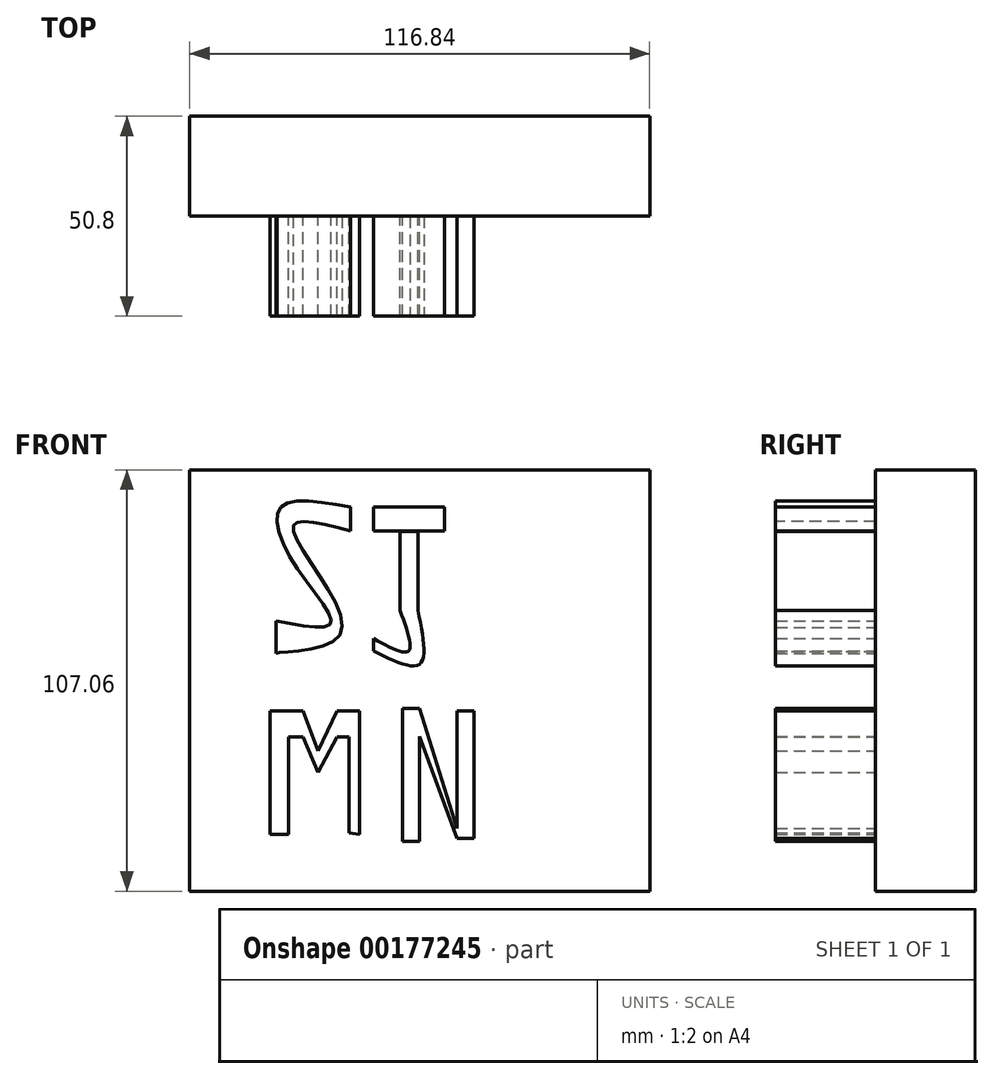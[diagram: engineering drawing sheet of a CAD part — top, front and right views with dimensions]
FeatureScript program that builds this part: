
annotation { "Feature Type Name" : "Feature", "Feature Type Description" : "" }
export const myFeature = defineFeature(function(context is Context, id is Id, definition is map)
    precondition{}
    {
        {
            var Q0;
            Q0=qCreatedBy(makeId("Front.planeOp"),FACE);
            var sketch = newSketch(context, id + "F0", { "sketchPlane" : qUnion([Q0])});
            skLineSegment(sketch, "E0.bottom", {"start": v(-58.42, -53.53) * mm, "end": v(58.42, -53.53) * mm});
            skLineSegment(sketch, "E0.top", {"start": v(-58.42, 53.53) * mm, "end": v(58.42, 53.53) * mm});
            skLineSegment(sketch, "E0.left", {"start": v(-58.42, -53.53) * mm, "end": v(-58.42, 53.53) * mm});
            skLineSegment(sketch, "E0.right", {"start": v(58.42, -53.53) * mm, "end": v(58.42, 53.53) * mm});
            skPoint(sketch, "E0.middle", {"position": v(0, 0) * mm});
            skSolve(sketch);
        }
        {
            var Q0;
            Q0 = qSketchRegion(id + "F0", true);
            extrude(context, id + "F1", {"entities" : qUnion([Q0]), "depth" : 25.4 * mm});
        }
        {
            var Q0;
            Q0=makeQuery(id+"F1.opExtrude","CAP_FACE",FACE,{"disambiguationData":[OSD([sQuery(id+"F0.wireOp",EDGE,"E0.bottom"),sQuery(id+"F0.wireOp",EDGE,"E0.top"),sQuery(id+"F0.wireOp",EDGE,"E0.left"),sQuery(id+"F0.wireOp",EDGE,"E0.right")])],"isStart":false});
            var sketch = newSketch(context, id + "F2", { "sketchPlane" : qUnion([Q0])});
            skFitSpline(sketch, "E1", {"points": [v(-17.56, 38) * mm, v(-32.23, 38.57) * mm, v(-20.15, 11.8) * mm, v(-36.55, 6.9) * mm, v(-36.26, 6.62) * mm], "startDerivative": vector(-81.22, 21.83) * mm, "endDerivative": vector(12.9, -6.86) * mm});
            skLineSegment(sketch, "E2", {"start": v(-17.56, 38) * mm, "end": v(-17.56, 44.03) * mm});
            skLineSegment(sketch, "E3", {"start": v(-36.55, 6.9) * mm, "end": v(-36.55, 15.16) * mm});
            skPoint(sketch, "E4.1.internal.orphan", {"position": v(-35.28, 44.03) * mm});
            skFitSpline(sketch, "E5", {"points": [v(-17.56, 44.03) * mm, v(-35.28, 44.03) * mm, v(-31.96, 29.73) * mm, v(-22.6, 14.54) * mm, v(-36.55, 15.16) * mm], "startDerivative": vector(-86.65, 15.67) * mm, "endDerivative": vector(-84.04, 16.75) * mm});
            skSolve(sketch);
        }
        {
            var Q0;
            {var subQ0=sQuery(id+"F2.wireOp",EDGE,"E2");Q0=makeQuery(id+"F2.imprint","IMPRINT",FACE,{"disambiguationData":[TD([[makeQuery(id+"F2.imprint","IMPRINT",EDGE,{"derivedFrom":subQ0}),1.0]])]});}
            extrude(context, id + "F3", {"entities" : qUnion([Q0]), "operationType" : NewBodyOperationType.ADD, "depth" : 25.4 * mm});
        }
        {
            var Q0;
            Q0=qCreatedBy(makeId("Front.planeOp"),FACE);
            var sketch = newSketch(context, id + "F4", { "sketchPlane" : qUnion([Q0])});
            skPoint(sketch, "E6.end.orphan", {"position": v(-6.26, 44.5) * mm});
            skPoint(sketch, "E6.start.orphan", {"position": v(0, 44.5) * mm});
            skPoint(sketch, "E7.end.orphan", {"position": v(-6.26, 41.34) * mm});
            skLineSegment(sketch, "E8.bottom", {"start": v(-11.73, 42.78) * mm, "end": v(15.9, 42.78) * mm});
            skLineSegment(sketch, "E8.top", {"start": v(-11.73, 38.16) * mm, "end": v(15.9, 38.16) * mm});
            skLineSegment(sketch, "E8.left", {"start": v(-11.73, 42.78) * mm, "end": v(-11.73, 38.16) * mm});
            skLineSegment(sketch, "E8.right", {"start": v(15.9, 42.78) * mm, "end": v(15.9, 38.16) * mm});
            skPoint(sketch, "E8.middle", {"position": v(2.09, 40.47) * mm});
            skPoint(sketch, "E9.0.internal.orphan", {"position": v(0, 38.16) * mm});
            skPoint(sketch, "E9.1.internal.orphan", {"position": v(0, 18.87) * mm});
            skPoint(sketch, "E9.2.internal.orphan", {"position": v(0, 11.96) * mm});
            skPoint(sketch, "E9.3.internal.orphan", {"position": v(0, 11.96) * mm});
            skLineSegment(sketch, "E10.bottom", {"start": v(2.43, 20.67) * mm, "end": v(-2.43, 20.67) * mm});
            skLineSegment(sketch, "E10.top", {"start": v(2.43, 38.13) * mm, "end": v(-2.43, 38.13) * mm});
            skLineSegment(sketch, "E10.left", {"start": v(2.43, 20.67) * mm, "end": v(2.43, 38.13) * mm});
            skLineSegment(sketch, "E10.right", {"start": v(-2.43, 20.67) * mm, "end": v(-2.43, 38.13) * mm});
            skPoint(sketch, "E10.middle", {"position": v(0, 29.4) * mm});
            skFitSpline(sketch, "E11", {"points": [v(2.43, 20.67) * mm, v(2.43, 9.03) * mm, v(-12.1, 6.13) * mm], "startDerivative": vector(6.44, -29.3) * mm, "endDerivative": vector(-34.68, -0.36) * mm});
            skLineSegment(sketch, "E12", {"start": v(-12.1, 6.13) * mm, "end": v(-12.1, 12.27) * mm});
            skFitSpline(sketch, "E13", {"points": [v(-12.1, 12.27) * mm, v(-3.38, 12.27) * mm, v(-2.43, 20.67) * mm], "startDerivative": vector(21.19, -4.27) * mm, "endDerivative": vector(-1.9, 21.13) * mm});
            skSolve(sketch);
        }
        {
            var Q0;
            Q0 = qSketchRegion(id + "F4", true);
            extrude(context, id + "F5", {"entities" : qUnion([Q0]), "operationType" : NewBodyOperationType.ADD, "depth" : 25.4 * mm});
        }
        {
            var Q0;
            Q0=makeQuery(id+"F1.opExtrude","CAP_FACE",FACE,{"disambiguationData":[OSD([sQuery(id+"F0.wireOp",EDGE,"E0.bottom"),sQuery(id+"F0.wireOp",EDGE,"E0.top"),sQuery(id+"F0.wireOp",EDGE,"E0.left"),sQuery(id+"F0.wireOp",EDGE,"E0.right")])],"isStart":false});
            var sketch = newSketch(context, id + "F6", { "sketchPlane" : qUnion([Q0])});
            skLineSegment(sketch, "E14.bottom", {"start": v(-11.8, 38) * mm, "end": v(6.3, 38) * mm});
            skLineSegment(sketch, "E14.top", {"start": v(-11.8, 44.1) * mm, "end": v(6.3, 44.1) * mm});
            skLineSegment(sketch, "E14.left", {"start": v(-11.8, 38) * mm, "end": v(-11.8, 44.1) * mm});
            skLineSegment(sketch, "E14.right", {"start": v(6.3, 38) * mm, "end": v(6.3, 44.1) * mm});
            skPoint(sketch, "E14.middle", {"position": v(-2.75, 41.05) * mm});
            skLineSegment(sketch, "E15.bottom", {"start": v(-5, 17.77) * mm, "end": v(-0.49, 17.77) * mm});
            skLineSegment(sketch, "E15.top", {"start": v(-5, 37.81) * mm, "end": v(-0.49, 37.81) * mm});
            skLineSegment(sketch, "E15.left", {"start": v(-5, 17.77) * mm, "end": v(-5, 37.81) * mm});
            skLineSegment(sketch, "E15.right", {"start": v(-0.49, 17.77) * mm, "end": v(-0.49, 37.81) * mm});
            skPoint(sketch, "E15.middle", {"position": v(-2.74, 27.8) * mm});
            skPoint(sketch, "E16.1.internal.orphan", {"position": v(0, 4.19) * mm});
            skFitSpline(sketch, "E17", {"points": [v(-0.49, 17.77) * mm, v(0, 4.19) * mm, v(-11.8, 7.48) * mm], "startDerivative": vector(7.4, -35) * mm, "endDerivative": vector(-30.35, 14.86) * mm});
            skLineSegment(sketch, "E18", {"start": v(-11.8, 7.48) * mm, "end": v(-11.8, 10.65) * mm});
            skFitSpline(sketch, "E19", {"points": [v(-11.8, 10.65) * mm, v(-2.88, 7.48) * mm, v(-5, 17.77) * mm], "startDerivative": vector(23.78, -12.97) * mm, "endDerivative": vector(-9.9, 26.86) * mm});
            skSolve(sketch);
        }
        {
            var Q0;
            Q0 = qSketchRegion(id + "F6", true);
            extrude(context, id + "F7", {"entities" : qUnion([Q0]), "operationType" : NewBodyOperationType.ADD, "depth" : 25.4 * mm});
        }
        {
            var Q0;
            Q0=makeQuery(id+"F1.opExtrude","CAP_FACE",FACE,{"disambiguationData":[OSD([sQuery(id+"F0.wireOp",EDGE,"E0.bottom"),sQuery(id+"F0.wireOp",EDGE,"E0.top"),sQuery(id+"F0.wireOp",EDGE,"E0.left"),sQuery(id+"F0.wireOp",EDGE,"E0.right")])],"isStart":false});
            var sketch = newSketch(context, id + "F8", { "sketchPlane" : qUnion([Q0])});
            skLineSegment(sketch, "E20", {"start": v(-38, -7.77) * mm, "end": v(-38, -39.14) * mm});
            skLineSegment(sketch, "E21", {"start": v(-38, -39.14) * mm, "end": v(-38, -7.77) * mm});
            skLineSegment(sketch, "E22", {"start": v(-38, -7.77) * mm, "end": v(-29.64, -7.77) * mm});
            skLineSegment(sketch, "E23", {"start": v(-29.64, -7.77) * mm, "end": v(-25.9, -17.84) * mm});
            skLineSegment(sketch, "E24", {"start": v(-25.9, -17.84) * mm, "end": v(-21, -7.77) * mm});
            skLineSegment(sketch, "E25", {"start": v(-21, -7.77) * mm, "end": v(-15.25, -7.77) * mm});
            skLineSegment(sketch, "E26", {"start": v(-15.25, -7.77) * mm, "end": v(-15.25, -39.14) * mm});
            skLineSegment(sketch, "E27", {"start": v(-15.25, -39.14) * mm, "end": v(-14.68, -37.41) * mm});
            skLineSegment(sketch, "E28", {"start": v(-38, -39.14) * mm, "end": v(-33.39, -39.14) * mm});
            skLineSegment(sketch, "E29", {"start": v(-33.39, -39.14) * mm, "end": v(-33.39, -14.4) * mm});
            skLineSegment(sketch, "E30", {"start": v(-33.39, -14.4) * mm, "end": v(-29.64, -14.4) * mm});
            skLineSegment(sketch, "E31", {"start": v(-29.64, -14.4) * mm, "end": v(-25.9, -23.31) * mm});
            skLineSegment(sketch, "E32", {"start": v(-25.9, -23.31) * mm, "end": v(-21, -14.4) * mm});
            skPoint(sketch, "E33.end.orphan", {"position": v(-15.25, -14.4) * mm});
            skLineSegment(sketch, "E34", {"start": v(-21, -14.4) * mm, "end": v(-18, -14.4) * mm});
            skLineSegment(sketch, "E35", {"start": v(-18, -38.7) * mm, "end": v(-15.25, -39.14) * mm});
            skLineSegment(sketch, "E36", {"start": v(-18, -14.4) * mm, "end": v(-18, -38.7) * mm});
            skLineSegment(sketch, "E37.bottom", {"start": v(0, -7.05) * mm, "end": v(-4.4, -7.05) * mm});
            skLineSegment(sketch, "E37.top", {"start": v(0, -40.86) * mm, "end": v(-4.4, -40.86) * mm});
            skLineSegment(sketch, "E37.left", {"start": v(0, -7.05) * mm, "end": v(0, -40.86) * mm});
            skLineSegment(sketch, "E37.right", {"start": v(-4.4, -7.05) * mm, "end": v(-4.4, -40.86) * mm});
            skLineSegment(sketch, "E38.bottom", {"start": v(13.73, -7.77) * mm, "end": v(9.4, -7.77) * mm});
            skLineSegment(sketch, "E38.top", {"start": v(13.73, -40.14) * mm, "end": v(9.4, -40.14) * mm});
            skLineSegment(sketch, "E38.left", {"start": v(13.73, -7.77) * mm, "end": v(13.73, -40.14) * mm});
            skLineSegment(sketch, "E38.right", {"start": v(9.4, -7.77) * mm, "end": v(9.4, -40.14) * mm});
            skLineSegment(sketch, "E39", {"start": v(0, -7.05) * mm, "end": v(9.4, -37.55) * mm});
            skLineSegment(sketch, "E40", {"start": v(0, -14.24) * mm, "end": v(9.4, -40.14) * mm});
            skSolve(sketch);
        }
        {
            var Q0;
            Q0 = qSketchRegion(id + "F8", true);
            extrude(context, id + "F9", {"entities" : qUnion([Q0]), "operationType" : NewBodyOperationType.ADD, "depth" : 25.4 * mm});
        }
    });
